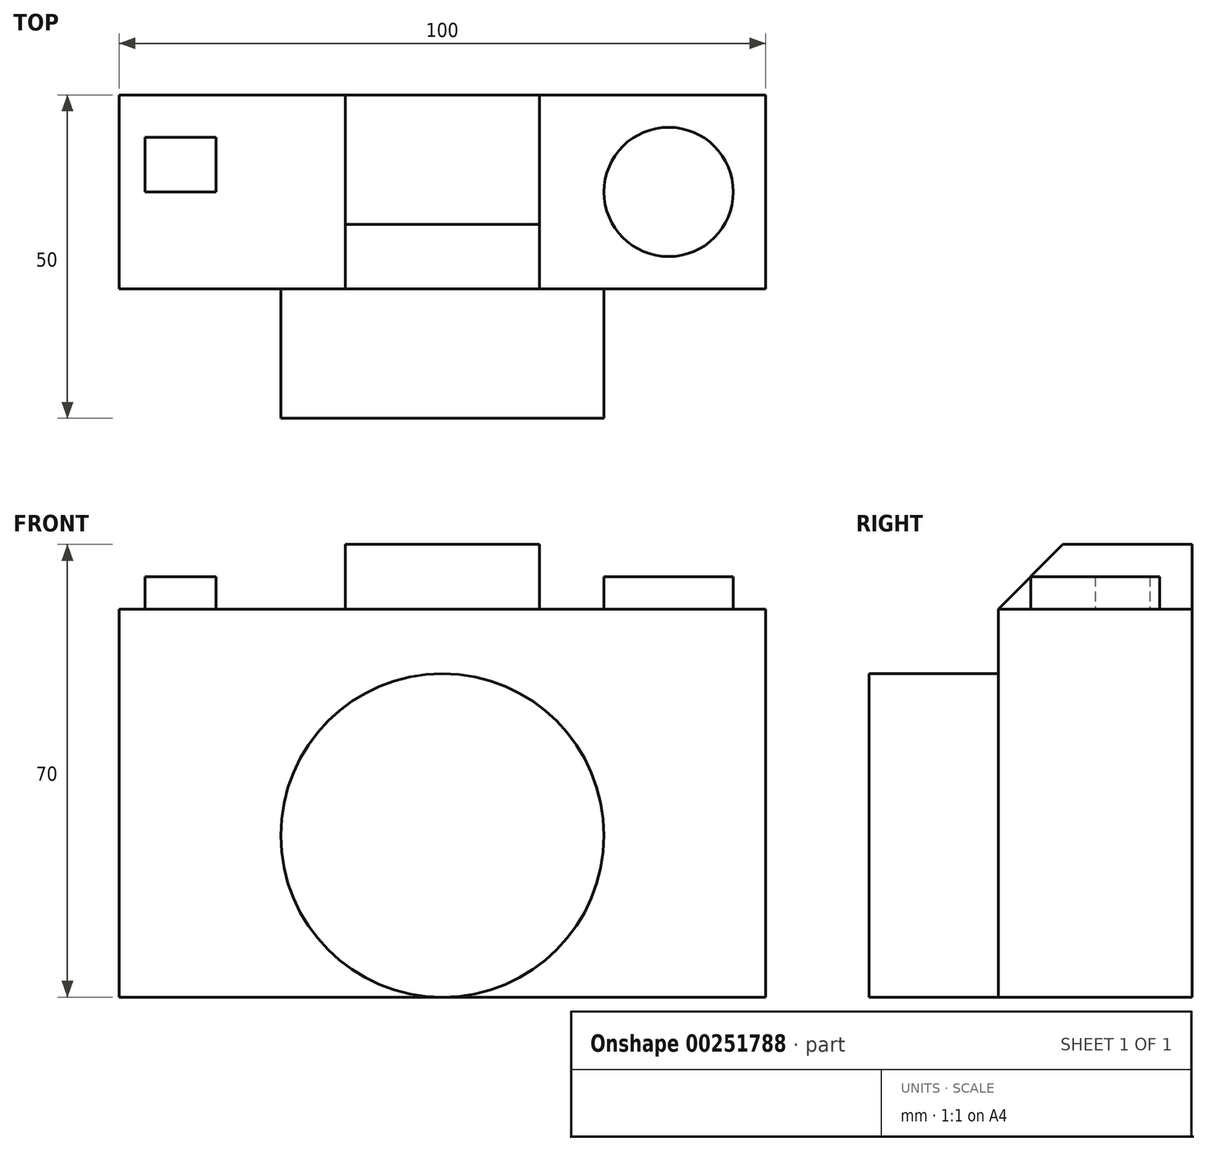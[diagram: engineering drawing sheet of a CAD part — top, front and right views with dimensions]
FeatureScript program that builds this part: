
annotation { "Feature Type Name" : "Feature", "Feature Type Description" : "" }
export const myFeature = defineFeature(function(context is Context, id is Id, definition is map)
    precondition{}
    {
        {
            var Q0;
            Q0=qCreatedBy(makeId("Front.planeOp"),FACE);
            var sketch = newSketch(context, id + "F0", { "sketchPlane" : qUnion([Q0])});
            skLineSegment(sketch, "E0.bottom", {"start": v(50, -25) * mm, "end": v(-50, -25) * mm});
            skLineSegment(sketch, "E0.top", {"start": v(50, 25) * mm, "end": v(-50, 25) * mm});
            skLineSegment(sketch, "E0.left", {"start": v(50, -25) * mm, "end": v(50, 25) * mm});
            skLineSegment(sketch, "E0.right", {"start": v(-50, -25) * mm, "end": v(-50, 25) * mm});
            skPoint(sketch, "E0.middle", {"position": v(0, 0) * mm});
            skSolve(sketch);
        }
        {
            var Q0;
            Q0 = qSketchRegion(id + "F0", true);
            extrude(context, id + "F1", {"entities" : qUnion([Q0]), "endBound" : BoundingType.SYMMETRIC, "depth" : 30 * mm});
        }
        {
            var Q0;
            Q0=makeQuery(id+"F1.opExtrude","SWEPT_FACE",FACE,{"disambiguationData":[OSD([sQuery(id+"F0.wireOp",EDGE,"E0.left")])]});
            var sketch = newSketch(context, id + "F2", { "sketchPlane" : qUnion([Q0])});
            skLineSegment(sketch, "E1.bottom", {"start": v(-15, 25) * mm, "end": v(15, 25) * mm});
            skLineSegment(sketch, "E1.top", {"start": v(-15, 35) * mm, "end": v(15, 35) * mm});
            skLineSegment(sketch, "E1.left", {"start": v(-15, 25) * mm, "end": v(-15, 35) * mm});
            skLineSegment(sketch, "E1.right", {"start": v(15, 25) * mm, "end": v(15, 35) * mm});
            skSolve(sketch);
        }
        {
            var Q0;
            Q0=makeQuery(id+"F1.opExtrude","CAP_FACE",FACE,{"disambiguationData":[OSD([sQuery(id+"F0.wireOp",EDGE,"E0.bottom"),sQuery(id+"F0.wireOp",EDGE,"E0.top"),sQuery(id+"F0.wireOp",EDGE,"E0.left"),sQuery(id+"F0.wireOp",EDGE,"E0.right")])],"isStart":false});
            var sketch = newSketch(context, id + "F3", { "sketchPlane" : qUnion([Q0])});
            skCircle(sketch, "E2", {"center": v(0, 0) * mm, "radius": 25 * mm});
            skSolve(sketch);
        }
        {
            var Q0;
            Q0 = qSketchRegion(id + "F3", true);
            extrude(context, id + "F4", {"entities" : qUnion([Q0]), "operationType" : NewBodyOperationType.ADD, "depth" : 20 * mm});
        }
        {
            var Q0;
            Q0 = qSketchRegion(id + "F2", true);
            extrude(context, id + "F5", {"entities" : qUnion([Q0]), "operationType" : NewBodyOperationType.ADD, "oppositeDirection" : true, "depth" : 100 * mm});
        }
        {
            var Q0;
            Q0=makeQuery(id+"F5.opExtrude","SWEPT_FACE",FACE,{"disambiguationData":[OSD([sQuery(id+"F2.wireOp",EDGE,"E1.top")])]});
            var sketch = newSketch(context, id + "F6", { "sketchPlane" : qUnion([Q0])});
            skCircle(sketch, "E3", {"center": v(35, 0) * mm, "radius": 10 * mm});
            skSolve(sketch);
        }
        {
            var Q0;
            Q0 = qSketchRegion(id + "F6", true);
            extrude(context, id + "F7", {"entities" : qUnion([Q0]), "operationType" : NewBodyOperationType.ADD, "depth" : 5 * mm});
        }
        {
            var Q0;
            Q0=makeQuery(id+"F5.opExtrude","SWEPT_FACE",FACE,{"disambiguationData":[OSD([sQuery(id+"F2.wireOp",EDGE,"E1.top")])]});
            var sketch = newSketch(context, id + "F8", { "sketchPlane" : qUnion([Q0])});
            skLineSegment(sketch, "E4.bottom", {"start": v(-46.01, 0) * mm, "end": v(-35, 0) * mm});
            skLineSegment(sketch, "E4.top", {"start": v(-46.01, 8.45) * mm, "end": v(-35, 8.45) * mm});
            skLineSegment(sketch, "E4.left", {"start": v(-46.01, 0) * mm, "end": v(-46.01, 8.45) * mm});
            skLineSegment(sketch, "E4.right", {"start": v(-35, 0) * mm, "end": v(-35, 8.45) * mm});
            skSolve(sketch);
        }
        {
            var Q0;
            Q0 = qSketchRegion(id + "F8", true);
            extrude(context, id + "F9", {"entities" : qUnion([Q0]), "operationType" : NewBodyOperationType.ADD, "depth" : 5 * mm});
        }
        {
            var Q0;
            Q0=makeQuery(id+"F5.opExtrude","SWEPT_FACE",FACE,{"disambiguationData":[OSD([sQuery(id+"F2.wireOp",EDGE,"E1.top")])]});
            var sketch = newSketch(context, id + "F10", { "sketchPlane" : qUnion([Q0])});
            skLineSegment(sketch, "E5.bottom", {"start": v(-15, 15) * mm, "end": v(15, 15) * mm});
            skLineSegment(sketch, "E5.top", {"start": v(-15, -15) * mm, "end": v(15, -15) * mm});
            skLineSegment(sketch, "E5.left", {"start": v(-15, 15) * mm, "end": v(-15, -15) * mm});
            skLineSegment(sketch, "E5.right", {"start": v(15, 15) * mm, "end": v(15, -15) * mm});
            skSolve(sketch);
        }
        {
            var Q0;
            Q0 = qSketchRegion(id + "F10", true);
            extrude(context, id + "F11", {"entities" : qUnion([Q0]), "operationType" : NewBodyOperationType.ADD, "depth" : 10 * mm});
        }
        {
            var Q0;
            Q0=makeQuery(id+"F11.opExtrude","SWEPT_FACE",FACE,{"disambiguationData":[OSD([sQuery(id+"F10.wireOp",EDGE,"E5.right")])]});
            var sketch = newSketch(context, id + "F12", { "sketchPlane" : qUnion([Q0])});
            skLineSegment(sketch, "E6", {"start": v(-15, 35) * mm, "end": v(-5, 45) * mm});
            skLineSegment(sketch, "E7.0", {"start": v(-15, 45) * mm, "end": v(-15, 35) * mm});
            skLineSegment(sketch, "E8.0", {"start": v(-5, 45) * mm, "end": v(-15, 45) * mm});
            skPoint(sketch, "E9.orphan", {"position": v(15, 45) * mm});
            skSolve(sketch);
        }
        {
            var Q0;
            Q0 = qSketchRegion(id + "F12", true);
            extrude(context, id + "F13", {"entities" : qUnion([Q0]), "operationType" : NewBodyOperationType.REMOVE, "endBound" : BoundingType.THROUGH_ALL, "oppositeDirection" : true, "depth" : 25 * mm});
        }
    });
